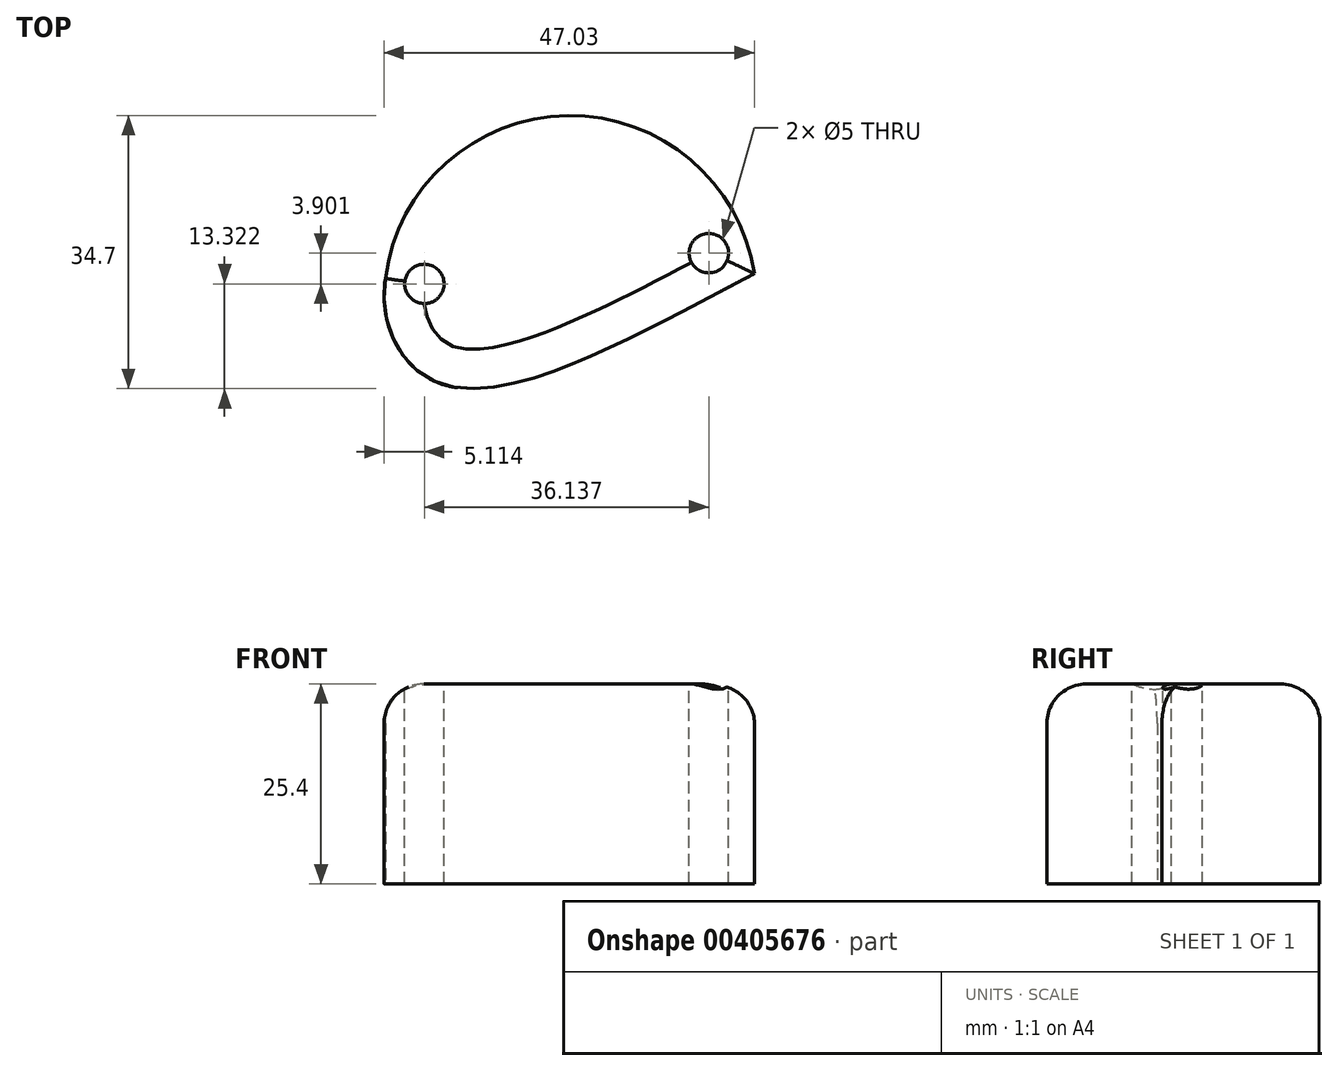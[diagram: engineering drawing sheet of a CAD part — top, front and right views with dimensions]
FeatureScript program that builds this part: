
annotation { "Feature Type Name" : "Feature", "Feature Type Description" : "" }
export const myFeature = defineFeature(function(context is Context, id is Id, definition is map)
    precondition{}
    {
        {
            var Q0;
            Q0=qCreatedBy(makeId("Top.planeOp"),FACE);
            var sketch = newSketch(context, id + "F0", { "sketchPlane" : qUnion([Q0])});
            skArc(sketch, "E0", {"start": v(-9.1, 21.2) * mm, "mid": v(-32.8, 41.28) * mm, "end": v(-55.98, 20.6) * mm});
            skFitSpline(sketch, "E1", {"points": [v(-55.98, 20.6) * mm, v(-48.81, 7.17) * mm, v(-9.1, 21.2) * mm], "startDerivative": vector(-7.31, -46.74) * mm, "endDerivative": vector(77.48, 40.66) * mm});
            skSolve(sketch);
        }
        {
            var Q0;
            Q0 = qSketchRegion(id + "F0", true);
            extrude(context, id + "F1", {"entities" : qUnion([Q0]), "depth" : 25.4 * mm});
        }
        {
            var Q0;
            Q0=makeQuery(id+"F1.opExtrude","CAP_EDGE",EDGE,{"disambiguationData":[OSD([sQuery(id+"F0.wireOp",EDGE,"E1")])],"isStart":false});
            var Q1;
            Q1=makeQuery(id+"F1.opExtrude","CAP_EDGE",EDGE,{"disambiguationData":[OSD([sQuery(id+"F0.wireOp",EDGE,"E0")])],"isStart":false});
            fillet(context, id + "F2", {"entities" : qUnion([Q0, Q1]), "radius" : 5 * mm, "tangentPropagation" : true, "allowEdgeOverflow" : false});
        }
        {
            var Q0;
            Q0=makeQuery(id+"F1.opExtrude","CAP_FACE",FACE,{"disambiguationData":[OSD([sQuery(id+"F0.wireOp",EDGE,"E0"),sQuery(id+"F0.wireOp",EDGE,"E1")])],"isStart":false});
            var sketch = newSketch(context, id + "F3", { "sketchPlane" : qUnion([Q0])});
            skCircle(sketch, "E2", {"center": v(-14.89, 23.8) * mm, "radius": 2.64 * mm});
            skCircle(sketch, "E3", {"center": v(-51.03, 19.9) * mm, "radius": 2.95 * mm});
            skSolve(sketch);
        }
        {
            var Q0;
            Q0=sQuery(id+"F3.wireOp",VERTEX,"E3.center");
            var Q1;
            Q1=sQuery(id+"F3.wireOp",VERTEX,"E2.center");
            var Q2;
            Q2=makeQuery(id+"F1.opExtrude","SWEPT_BODY",BODY,{"disambiguationData":[OSD([sQuery(id+"F0.wireOp",EDGE,"E0"),sQuery(id+"F0.wireOp",EDGE,"E1")])]});
            hole(context, id + "F4", {"style" : HoleStyle.SIMPLE, "endStyle" : HoleEndStyle.THROUGH, "holeDiameter" : 5 * mm, "isTappedThrough" : true, "tappedDepth" : 12 * mm, "tapClearance" : 3, "locations" : qUnion([Q0, Q1]), "scope" : qUnion([Q2])});
        }
    });
